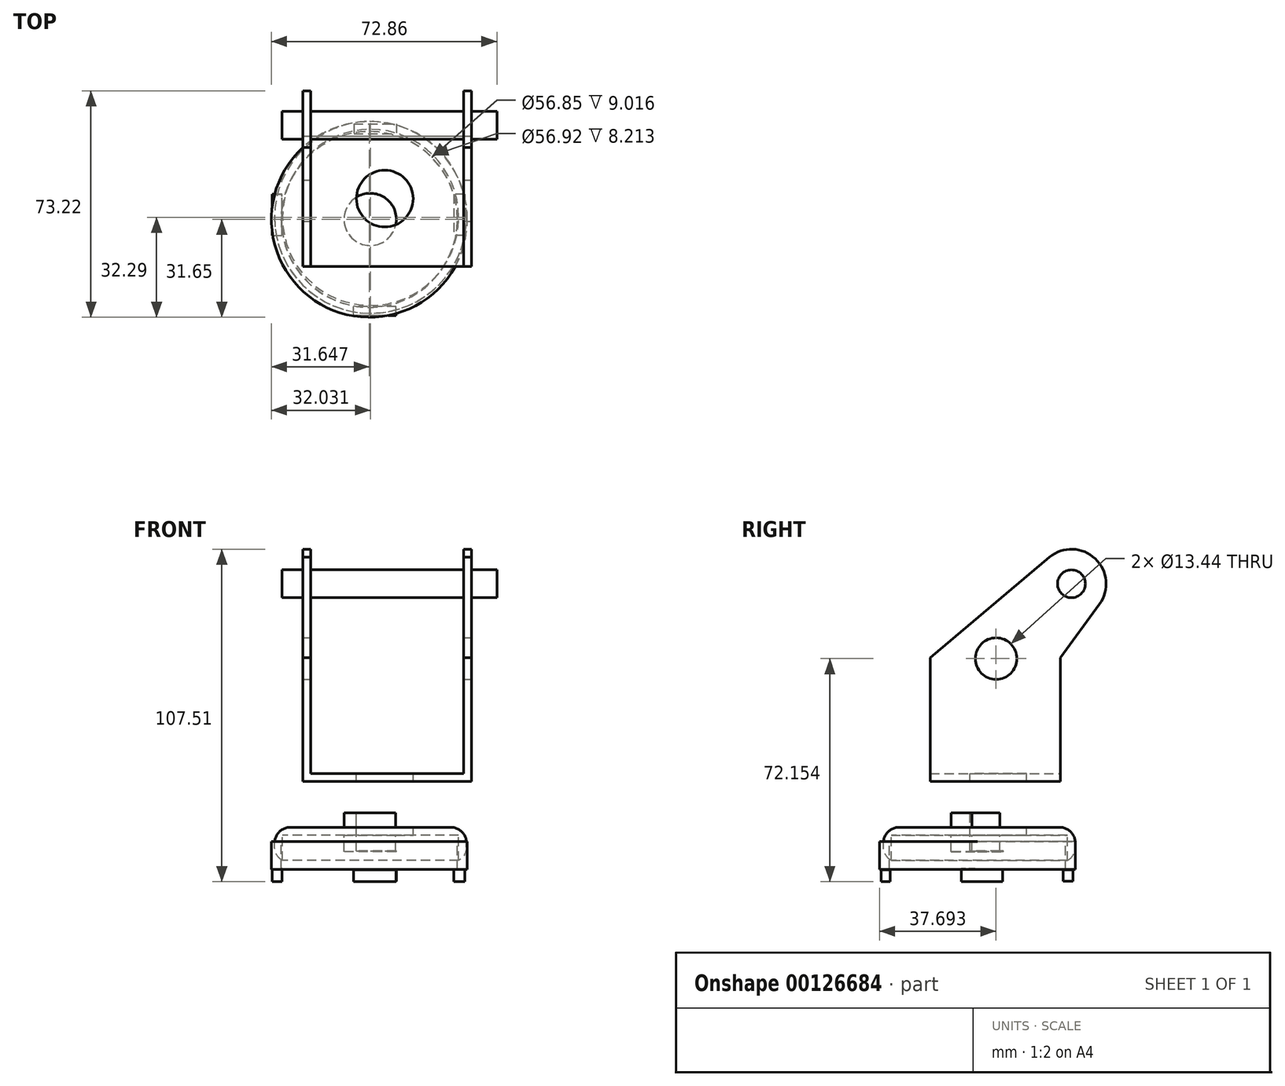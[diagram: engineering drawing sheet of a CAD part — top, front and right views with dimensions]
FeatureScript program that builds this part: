
annotation { "Feature Type Name" : "Feature", "Feature Type Description" : "" }
export const myFeature = defineFeature(function(context is Context, id is Id, definition is map)
    precondition{}
    {
        {
            var Q0;
            Q0=qCreatedBy(makeId("Right.planeOp"),FACE);
            var sketch = newSketch(context, id + "F0", { "sketchPlane" : qUnion([Q0])});
            skLineSegment(sketch, "E0", {"start": v(-28.17, 26.72) * mm, "end": v(-28.17, -13.28) * mm});
            skLineSegment(sketch, "E1", {"start": v(13.83, 26.72) * mm, "end": v(13.83, -13.28) * mm});
            skLineSegment(sketch, "E2", {"start": v(-28.17, -13.28) * mm, "end": v(13.83, -13.28) * mm});
            skLineSegment(sketch, "E3", {"start": v(-28.17, 26.72) * mm, "end": v(10.37, 59.26) * mm});
            skLineSegment(sketch, "E4", {"start": v(13.83, 26.72) * mm, "end": v(26.48, 44.02) * mm});
            skArc(sketch, "E5", {"start": v(26.48, 44.02) * mm, "mid": v(25.14, 58.73) * mm, "end": v(10.37, 59.26) * mm});
            skSolve(sketch);
        }
        {
            var Q0;
            Q0=makeQuery(id+"F0.imprint","IMPRINT",FACE,{"disambiguationData":[TD([[makeQuery(id+"F0.imprint","IMPRINT",EDGE,{"derivedFrom":sQuery(id+"F0.wireOp",EDGE,"E0")}),1.0]])]});
            var Q1;
            Q1=makeQuery(id+"F0.imprint","IMPRINT",FACE,{"disambiguationData":[TD([[makeQuery(id+"F0.imprint","IMPRINT",EDGE,{"derivedFrom":sQuery(id+"F0.wireOp",EDGE,"mzePpVeE-JAXA-lHZw-7vVi-UwVuHMDZnZBT")}),1.0]])]});
            extrude(context, id + "F1", {"entities" : qUnion([Q0, Q1]), "depth" : 50.5 * mm, "hasSecondDirection" : true, "secondDirectionOppositeDirection" : true, "secondDirectionDepth" : 4 * mm});
        }
        {
            var Q0;
            Q0=qCreatedBy(makeId("Top.planeOp"),FACE);
            var sketch = newSketch(context, id + "F2", { "sketchPlane" : qUnion([Q0])});
            skCircle(sketch, "E6", {"center": v(17.9, -12.29) * mm, "radius": 31 * mm});
            skSolve(sketch);
        }
        {
            var Q0;
            Q0 = qSketchRegion(id + "F2", true);
            extrude(context, id + "F3", {"entities" : qUnion([Q0]), "operationType" : NewBodyOperationType.ADD, "oppositeDirection" : true, "depth" : 38.86 * mm, "hasSecondDirection" : true, "secondDirectionOppositeDirection" : true, "secondDirectionDepth" : 28.1 * mm});
        }
        {
            var Q0;
            Q0=makeQuery(id+"F3.opExtrude","CAP_FACE",FACE,{"disambiguationData":[OSD([sQuery(id+"F2.wireOp",EDGE,"E6")])],"isStart":false});
            shell(context, id + "F4", {"entities" : qUnion([Q0]), "thickness" : 2.54 * mm});
        }
        {
            var Q0;
            Q0=qCreatedBy(makeId("Top.planeOp"),FACE);
            var sketch = newSketch(context, id + "F5", { "sketchPlane" : qUnion([Q0])});
            skCircle(sketch, "E7", {"center": v(17.77, -12.93) * mm, "radius": 8.45 * mm});
            skSolve(sketch);
        }
        {
            var Q0;
            Q0 = qSketchRegion(id + "F5", true);
            extrude(context, id + "F6", {"entities" : qUnion([Q0]), "operationType" : NewBodyOperationType.ADD, "oppositeDirection" : true, "depth" : 36.05 * mm, "hasSecondDirection" : true, "secondDirectionOppositeDirection" : true, "secondDirectionDepth" : 23.5 * mm});
        }
        {
            var Q0;
            Q0=qCreatedBy(makeId("Top.planeOp"),FACE);
            var sketch = newSketch(context, id + "F7", { "sketchPlane" : qUnion([Q0])});
            skCircle(sketch, "E8", {"center": v(17.52, -12.93) * mm, "radius": 31.65 * mm});
            skCircle(sketch, "E9", {"center": v(17.52, -12.93) * mm, "radius": 28.42 * mm});
            skSolve(sketch);
        }
        {
            var Q0;
            Q0 = qSketchRegion(id + "F7", true);
            extrude(context, id + "F8", {"entities" : qUnion([Q0]), "oppositeDirection" : true, "depth" : 41.73 * mm, "hasSecondDirection" : true, "secondDirectionOppositeDirection" : true, "secondDirectionDepth" : 32.72 * mm});
        }
        {
            var Q0;
            Q0=qCreatedBy(makeId("Front.planeOp"),FACE);
            var sketch = newSketch(context, id + "F9", { "sketchPlane" : qUnion([Q0])});
            skLineSegment(sketch, "E10", {"start": v(12.51, -41.84) * mm, "end": v(12.51, -45.6) * mm});
            skLineSegment(sketch, "E11", {"start": v(12.51, -45.6) * mm, "end": v(24.2, -45.6) * mm});
            skLineSegment(sketch, "E12", {"start": v(24.2, -45.6) * mm, "end": v(26.23, -45.6) * mm});
            skLineSegment(sketch, "E13", {"start": v(26.23, -45.6) * mm, "end": v(26.23, -41.84) * mm});
            skLineSegment(sketch, "E14", {"start": v(12.51, -41.84) * mm, "end": v(26.23, -41.84) * mm});
            skSolve(sketch);
        }
        {
            var Q0;
            Q0 = qSketchRegion(id + "F9", true);
            extrude(context, id + "F10", {"entities" : qUnion([Q0]), "oppositeDirection" : true, "depth" : 17.98 * mm, "hasSecondDirection" : true, "secondDirectionOppositeDirection" : true, "secondDirectionDepth" : 14.78 * mm});
        }
        {
            var Q0;
            Q0=qCreatedBy(makeId("Front.planeOp"),FACE);
            var sketch = newSketch(context, id + "F11", { "sketchPlane" : qUnion([Q0])});
            skLineSegment(sketch, "E15", {"start": v(26.17, -41.85) * mm, "end": v(26.17, -45.64) * mm});
            skLineSegment(sketch, "E16", {"start": v(26.17, -45.64) * mm, "end": v(12.44, -45.64) * mm});
            skLineSegment(sketch, "E17", {"start": v(12.44, -45.64) * mm, "end": v(12.44, -41.62) * mm});
            skLineSegment(sketch, "E18", {"start": v(26.17, -41.85) * mm, "end": v(12.44, -41.85) * mm});
            skSolve(sketch);
        }
        {
            var Q0;
            Q0 = qSketchRegion(id + "F11", true);
            extrude(context, id + "F12", {"entities" : qUnion([Q0]), "depth" : 44 * mm, "hasSecondDirection" : true, "secondDirectionOppositeDirection" : false, "secondDirectionDepth" : 41.05 * mm});
        }
        {
            var Q0;
            Q0=qCreatedBy(makeId("Right.planeOp"),FACE);
            var sketch = newSketch(context, id + "F13", { "sketchPlane" : qUnion([Q0])});
            skLineSegment(sketch, "E19", {"start": v(-18.1, -41.4) * mm, "end": v(-18.1, -45.72) * mm});
            skLineSegment(sketch, "E20", {"start": v(-18.1, -45.72) * mm, "end": v(-4.74, -45.72) * mm});
            skLineSegment(sketch, "E21", {"start": v(-4.74, -45.72) * mm, "end": v(-4.74, -41.46) * mm});
            skLineSegment(sketch, "E22", {"start": v(-18.1, -41.4) * mm, "end": v(-4.74, -41.46) * mm});
            skSolve(sketch);
        }
        {
            var Q0;
            Q0 = qSketchRegion(id + "F13", true);
            extrude(context, id + "F14", {"entities" : qUnion([Q0]), "operationType" : NewBodyOperationType.ADD, "oppositeDirection" : true, "depth" : 13.9 * mm, "hasSecondDirection" : true, "secondDirectionOppositeDirection" : true, "secondDirectionDepth" : 10.77 * mm});
        }
        {
            var Q0;
            Q0=qCreatedBy(makeId("Right.planeOp"),FACE);
            var sketch = newSketch(context, id + "F15", { "sketchPlane" : qUnion([Q0])});
            skLineSegment(sketch, "E23", {"start": v(-4.81, -45.63) * mm, "end": v(-18.12, -45.63) * mm});
            skLineSegment(sketch, "E24", {"start": v(-18.12, -45.63) * mm, "end": v(-18.12, -41.79) * mm});
            skLineSegment(sketch, "E25", {"start": v(-18.12, -41.79) * mm, "end": v(-4.81, -41.74) * mm});
            skLineSegment(sketch, "E26", {"start": v(-4.81, -41.74) * mm, "end": v(-4.81, -45.63) * mm});
            skSolve(sketch);
        }
        {
            var Q0;
            Q0 = qSketchRegion(id + "F15", true);
            extrude(context, id + "F16", {"entities" : qUnion([Q0]), "depth" : 48.35 * mm, "hasSecondDirection" : true, "secondDirectionOppositeDirection" : false, "secondDirectionDepth" : 44.83 * mm});
        }
        {
            var Q0;
            Q0=makeQuery(id+"F3.opExtrude","CAP_EDGE",EDGE,{"disambiguationData":[OSD([sQuery(id+"F2.wireOp",EDGE,"E6")])],"isStart":true});
            var Q1;
            Q1=makeQuery(id+"F3.opExtrude","CAP_EDGE",EDGE,{"disambiguationData":[OSD([sQuery(id+"F2.wireOp",EDGE,"E6")])],"isStart":false});
            fillet(context, id + "F17", {"entities" : qUnion([Q0, Q1]), "radius" : 5.08 * mm, "tangentPropagation" : true, "allowEdgeOverflow" : false});
        }
        {
            var Q0;
            Q0=makeQuery(id+"F1.opExtrude","SWEPT_FACE",FACE,{"disambiguationData":[OSD([sQuery(id+"F0.wireOp",EDGE,"E0")])]});
            var Q1;
            Q1=makeQuery(id+"F1.opExtrude","SWEPT_FACE",FACE,{"disambiguationData":[OSD([sQuery(id+"F0.wireOp",EDGE,"E3")])]});
            var Q2;
            Q2=makeQuery(id+"F1.opExtrude","SWEPT_FACE",FACE,{"disambiguationData":[OSD([sQuery(id+"F0.wireOp",EDGE,"E5")])]});
            var Q3;
            Q3=makeQuery(id+"F1.opExtrude","SWEPT_FACE",FACE,{"disambiguationData":[OSD([sQuery(id+"F0.wireOp",EDGE,"E4")])]});
            var Q4;
            Q4=makeQuery(id+"F1.opExtrude","SWEPT_FACE",FACE,{"disambiguationData":[OSD([sQuery(id+"F0.wireOp",EDGE,"E1")])]});
            shell(context, id + "F18", {"entities" : qUnion([Q0, Q1, Q2, Q3, Q4]), "thickness" : 2.5 * mm});
        }
        {
            var Q0;
            Q0=makeQuery(id+"F1.opExtrude","CAP_FACE",FACE,{"disambiguationData":[OSD([sQuery(id+"F0.wireOp",EDGE,"E0"),sQuery(id+"F0.wireOp",EDGE,"E1"),sQuery(id+"F0.wireOp",EDGE,"E2"),sQuery(id+"F0.wireOp",EDGE,"E3"),sQuery(id+"F0.wireOp",EDGE,"E4"),sQuery(id+"F0.wireOp",EDGE,"E5")])],"isStart":false});
            var sketch = newSketch(context, id + "F19", { "sketchPlane" : qUnion([Q0])});
            skCircle(sketch, "E27", {"center": v(17.46, 50.61) * mm, "radius": 4.5 * mm});
            skCircle(sketch, "E28", {"center": v(-6.89, 26.43) * mm, "radius": 6.72 * mm});
            skSolve(sketch);
        }
        {
            var Q0;
            Q0=makeQuery(id+"F19.imprint","IMPRINT",FACE,{"disambiguationData":[TD([[makeQuery(id+"F19.imprint","IMPRINT",EDGE,{"derivedFrom":sQuery(id+"F19.wireOp",EDGE,"E28")}),1.0]])]});
            extrude(context, id + "F20", {"entities" : qUnion([Q0]), "operationType" : NewBodyOperationType.REMOVE, "endBound" : BoundingType.THROUGH_ALL, "oppositeDirection" : true, "depth" : 25 * mm});
        }
        {
            var Q0;
            Q0=makeQuery(id+"F19.imprint","IMPRINT",FACE,{"disambiguationData":[TD([[makeQuery(id+"F19.imprint","IMPRINT",EDGE,{"derivedFrom":sQuery(id+"F19.wireOp",EDGE,"E27")}),1.0]])]});
            extrude(context, id + "F21", {"entities" : qUnion([Q0]), "operationType" : NewBodyOperationType.ADD, "oppositeDirection" : true, "depth" : 61.25 * mm, "hasSecondDirection" : true, "secondDirectionOppositeDirection" : false, "secondDirectionDepth" : 8.23 * mm});
        }
        {
            var Q0;
            Q0=makeQuery(id+"F18.opShell","OFFSET_FACE",FACE,{"disambiguationData":[OSD([sQuery(id+"F0.wireOp",EDGE,"E2")])]});
            var sketch = newSketch(context, id + "F22", { "sketchPlane" : qUnion([Q0])});
            skCircle(sketch, "E29", {"center": v(22.5, -6.2) * mm, "radius": 9.16 * mm});
            skSolve(sketch);
        }
        {
            var Q0;
            Q0 = qSketchRegion(id + "F22", true);
            extrude(context, id + "F23", {"entities" : qUnion([Q0]), "operationType" : NewBodyOperationType.REMOVE, "oppositeDirection" : true, "depth" : 25 * mm});
        }
    });
